# Revit family: Screens-Worksurface_Mounted-Teknion-JNSEFW-Fabric_Elevated-R20161
name_source: partatom
category: Furniture
revit_build: Autodesk Revit Architecture 2016 (Build: 20150714_1515(x64)
units: mm (PartAtom-declared; Revit-internal decimal feet)

## family parameters
Always vertical = Yes
Cut with Voids When Loaded = No
OmniClass Number = 23.40.20.00
OmniClass Title = General Furniture and Specialties
Room Calculation Point = No
Shared = Yes
Work Plane-Based = No

## types (4) — shared parameters
Assembly Code = E2020200
Manufacturer = Teknion
Manufacturer Fax = 416.661.4586
Part Number = JNSEFW
Product Documentation Link = http://www.teknion.com
Product Line = Expansion Cityline
Product Page URL = http://www.teknion.com
Series = Expansion Cityline
Sustainability Data = http://www.teknion.com
URL = www.teknion.com
Unit Weight URL = http://www.teknion.com
Warranty = http://www.teknion.com

## per-type parameters (varying)
| type | Description | Model |
| Standard Width | Fabric Elevated Screen - Worksurface Mounted, 10" Modesty Base, Standard Width | JNSEFW10__S |
| One Side - Left Width Extension | Fabric Elevated Screen - Worksurface Mounted, 10" Modesty Base, Left Side Width Extension | JNSEFW10__L |
| Both Sides Width Extension | Fabric Elevated Screen - Worksurface Mounted, 10" Modesty Base, Both Sides Width Extension | JNSEFW10__B |
| One Side - Right Width Extension | Fabric Elevated Screen - Worksurface Mounted, 10" Modesty Base, Right Side Width Extension | JNSEFW10__R |

type visibility flags: 4 boolean params named "<type name>" — each type sets only its own to Yes (folded from table)

## geometry (parser evidence)
native form markers: Sweep x1
no freeform markers — native parametric forms only
